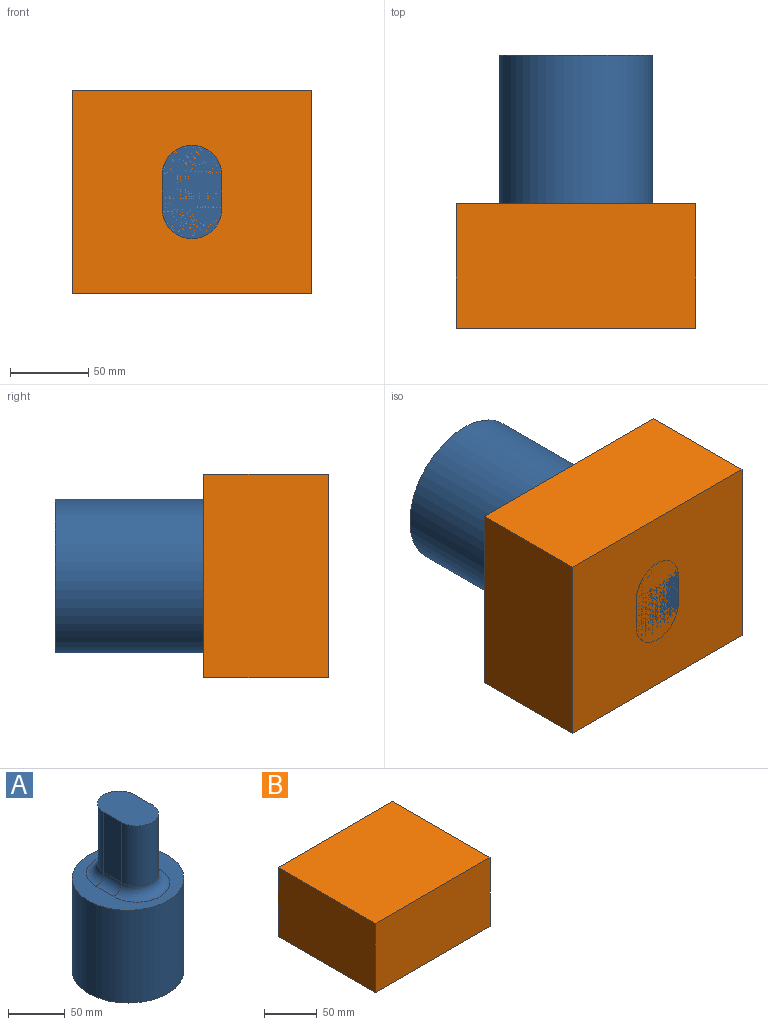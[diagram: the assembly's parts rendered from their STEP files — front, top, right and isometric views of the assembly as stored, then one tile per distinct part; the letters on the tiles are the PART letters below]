
ASSEMBLY  parts=2 mates=1
PART A: 12 faces, bbox 98.4x100.1x175 mm
  f0: cylinder r=49.19mm len=100mm, axis (0,0,-1), area 30908.3mm2, adj f1,f2
  f1: plane 98.38x98.38mm, normal (0,0,1), area 3684.1mm2, adj f0,f8,f9,f10,f11
  f2: plane 98.38x98.38mm, normal (0,0,-1), area 7602.2mm2, adj f0
  f3: plane 65x22mm, normal (1,0,0), area 1430mm2, adj f4,f6,f7,f9
  f4: cylinder r=19mm len=65mm, axis (0,0,-1), area 3879.9mm2, adj f3,f5,f7,f11
  f5: plane 65x22mm, normal (-1,0,0), area 1430mm2, adj f4,f6,f7,f10
  f6: cylinder r=19mm len=65mm, axis (0,0,-1), area 3879.9mm2, adj f3,f5,f7,f8
  f7: plane 60x38mm, normal (0,0,1), area 1970.1mm2, adj f3,f4,f5,f6
  f8: torus R=29mm, axis (0,0,1), area 1116.9mm2, adj f1,f6,f9,f10
  f9: cylinder r=10mm len=22mm, axis (0,1,0), area 345.6mm2, adj f1,f3,f8,f11
  f10: cylinder r=10mm len=22mm, axis (0,-1,0), area 345.6mm2, adj f1,f5,f8,f11
  f11: torus R=29mm, axis (0,0,1), area 1116.9mm2, adj f1,f4,f9,f10
PART B: 6 faces, bbox 153.6x130.3x80 mm
  f0: plane 130.35x80mm, normal (-1,0,0), area 10427.9mm2, adj f1,f3,f4,f5
  f1: plane 153.58x80mm, normal (0,-1,0), area 12286.6mm2, adj f0,f2,f4,f5
  f2: plane 130.35x80mm, normal (1,0,0), area 10427.9mm2, adj f1,f3,f4,f5
  f3: plane 153.58x80mm, normal (0,1,0), area 12286.6mm2, adj f0,f2,f4,f5
  f4: plane 153.58x130.35mm, normal (0,0,1), area 20019.3mm2, adj f0,f1,f2,f3
  f5: plane 153.58x130.35mm, normal (0,0,-1), area 20019.3mm2, adj f0,f1,f2,f3
PLACE A rot(axis=(1,0,0),90deg) t=(0,0,0)mm
PLACE B rot(axis=(-1,0,0),90deg) t=(-76.79,-175,65.17)mm
MATE planar B.f5 <-> A.f0  axis (0,-1,0) through (0,-175,0)mm
